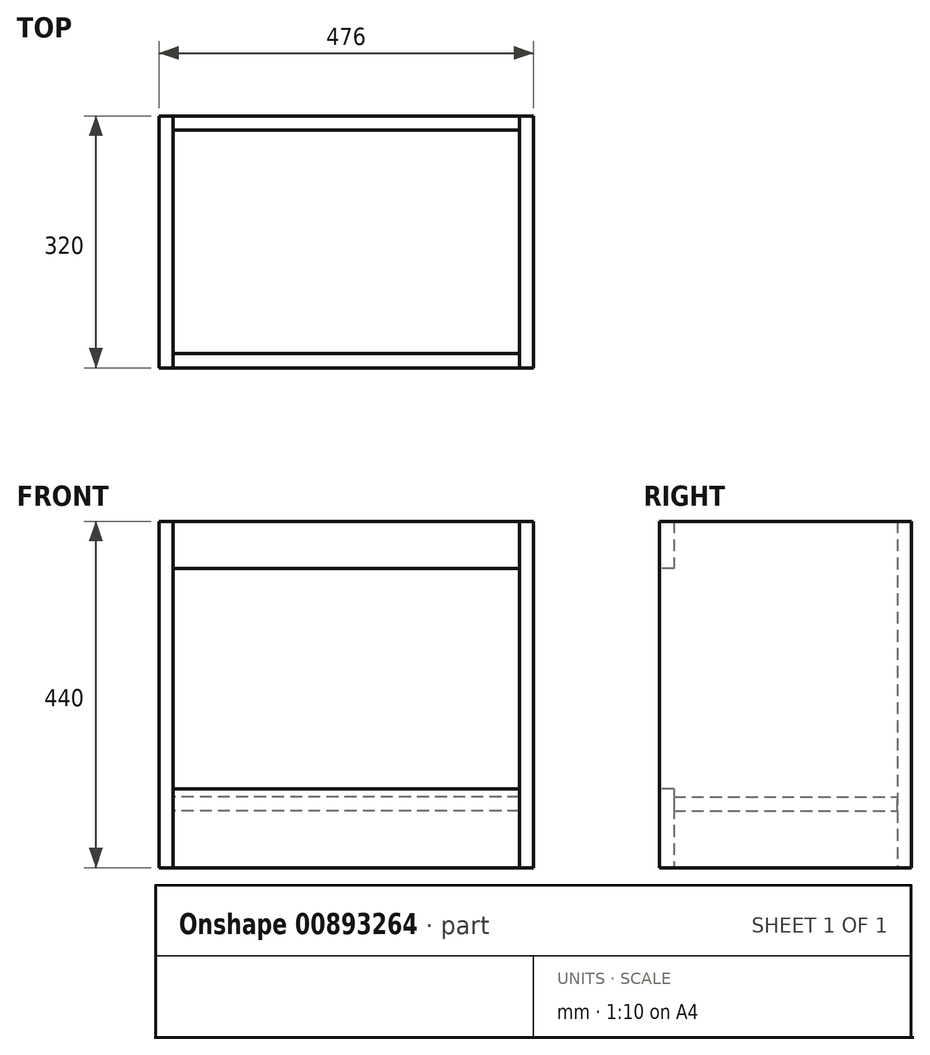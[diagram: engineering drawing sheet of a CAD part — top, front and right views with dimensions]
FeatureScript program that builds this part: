
annotation { "Feature Type Name" : "Feature", "Feature Type Description" : "" }
export const myFeature = defineFeature(function(context is Context, id is Id, definition is map)
    precondition{}
    {
        {
            var Q0;
            Q0=qCreatedBy(makeId("Top.planeOp"),FACE);
            var sketch = newSketch(context, id + "F0", { "sketchPlane" : qUnion([Q0])});
            skLineSegment(sketch, "E0.bottom", {"start": v(150, 100) * mm, "end": v(-150, 100) * mm, "construction": true});
            skLineSegment(sketch, "E0.top", {"start": v(150, -100) * mm, "end": v(-150, -100) * mm, "construction": true});
            skLineSegment(sketch, "E0.left", {"start": v(150, 100) * mm, "end": v(150, -100) * mm, "construction": true});
            skLineSegment(sketch, "E0.right", {"start": v(-150, 100) * mm, "end": v(-150, -100) * mm, "construction": true});
            skPoint(sketch, "E0.middle", {"position": v(0, 0) * mm});
            skLineSegment(sketch, "E1.bottom", {"start": v(-238, -140) * mm, "end": v(-220, -140) * mm});
            skLineSegment(sketch, "E1.top", {"start": v(-238, 180) * mm, "end": v(-220, 180) * mm});
            skLineSegment(sketch, "E1.left", {"start": v(-238, -140) * mm, "end": v(-238, 180) * mm});
            skLineSegment(sketch, "E1.right", {"start": v(-220, -140) * mm, "end": v(-220, 162) * mm});
            skLineSegment(sketch, "E2.MirrorCS", {"start": v(220, -140) * mm, "end": v(220, 162) * mm});
            skLineSegment(sketch, "E3.MirrorCS", {"start": v(238, -140) * mm, "end": v(220, -140) * mm});
            skLineSegment(sketch, "E4.MirrorCS", {"start": v(238, -140) * mm, "end": v(238, 180) * mm});
            skLineSegment(sketch, "E5.MirrorCS", {"start": v(238, 180) * mm, "end": v(220, 180) * mm});
            skLineSegment(sketch, "E6", {"start": v(-220, 180) * mm, "end": v(220, 180) * mm});
            skLineSegment(sketch, "E7", {"start": v(220, 162) * mm, "end": v(-220, 162) * mm});
            skLineSegment(sketch, "E8", {"start": v(-220, 162) * mm, "end": v(-220, 180) * mm});
            skLineSegment(sketch, "E9", {"start": v(220, 162) * mm, "end": v(220, 180) * mm});
            skLineSegment(sketch, "E10", {"start": v(-220, -140) * mm, "end": v(220, -140) * mm, "construction": true});
            skSolve(sketch);
        }
        {
            var Q0;
            Q0=makeQuery(id+"F0.imprint","IMPRINT",FACE,{"disambiguationData":[TD([[makeQuery(id+"F0.imprint","IMPRINT",EDGE,{"derivedFrom":sQuery(id+"F0.wireOp",EDGE,"E6")}),-1.0]])]});
            extrude(context, id + "F1", {"entities" : qUnion([Q0]), "depth" : 120 * mm, "offsetDistance" : 25 * mm, "hasSecondDirection" : true, "secondDirectionOppositeDirection" : true, "secondDirectionDepth" : 320 * mm});
        }
        {
            var Q0;
            Q0=makeQuery(id+"F0.imprint","IMPRINT",FACE,{"disambiguationData":[TD([[makeQuery(id+"F0.imprint","IMPRINT",EDGE,{"derivedFrom":sQuery(id+"F0.wireOp",EDGE,"E1.bottom")}),1.0]])]});
            var Q1;
            Q1=makeQuery(id+"F0.imprint","IMPRINT",FACE,{"disambiguationData":[TD([[makeQuery(id+"F0.imprint","IMPRINT",EDGE,{"derivedFrom":sQuery(id+"F0.wireOp",EDGE,"E2.MirrorCS")}),-1.0]])]});
            var Q2;
            Q2=makeQuery(id+"F1.opExtrude","CAP_FACE",FACE,{"disambiguationData":[OSD([sQuery(id+"F0.wireOp",EDGE,"E6"),sQuery(id+"F0.wireOp",EDGE,"E7"),sQuery(id+"F0.wireOp",EDGE,"E8"),sQuery(id+"F0.wireOp",EDGE,"E9")])],"isStart":false});
            var Q3;
            Q3=makeQuery(id+"F1.opExtrude","CAP_FACE",FACE,{"disambiguationData":[OSD([sQuery(id+"F0.wireOp",EDGE,"E6"),sQuery(id+"F0.wireOp",EDGE,"E7"),sQuery(id+"F0.wireOp",EDGE,"E8"),sQuery(id+"F0.wireOp",EDGE,"E9")])],"isStart":true});
            extrude(context, id + "F2", {"entities" : qUnion([Q0, Q1]), "endBound" : BoundingType.UP_TO_SURFACE, "depth" : 25 * mm, "endBoundEntityFace" : qUnion([Q2]), "offsetDistance" : 25 * mm, "hasSecondDirection" : true, "secondDirectionBound" : SecondDirectionBoundingType.UP_TO_SURFACE, "secondDirectionOppositeDirection" : true, "secondDirectionDepth" : 25 * mm, "secondDirectionBoundEntityFace" : qUnion([Q3])});
        }
        {
            var Q0;
            Q0=qCreatedBy(makeId("Right.planeOp"),FACE);
            var sketch = newSketch(context, id + "F3", { "sketchPlane" : qUnion([Q0])});
            skLineSegment(sketch, "E11.bottom", {"start": v(162, -230) * mm, "end": v(-122, -230) * mm});
            skLineSegment(sketch, "E11.top", {"start": v(162, -248) * mm, "end": v(-122, -248) * mm});
            skLineSegment(sketch, "E11.left", {"start": v(162, -230) * mm, "end": v(162, -248) * mm});
            skLineSegment(sketch, "E12.bottom", {"start": v(-140, -320) * mm, "end": v(-122, -320) * mm});
            skLineSegment(sketch, "E12.top", {"start": v(-140, -220) * mm, "end": v(-122, -220) * mm});
            skLineSegment(sketch, "E12.left", {"start": v(-140, -320) * mm, "end": v(-140, -220) * mm});
            skLineSegment(sketch, "E12.right", {"start": v(-122, -320) * mm, "end": v(-122, -220) * mm});
            skLineSegment(sketch, "E13.bottom", {"start": v(-140, 60) * mm, "end": v(-122, 60) * mm});
            skLineSegment(sketch, "E13.top", {"start": v(-140, 120) * mm, "end": v(-122, 120) * mm});
            skLineSegment(sketch, "E13.left", {"start": v(-140, 60) * mm, "end": v(-140, 120) * mm});
            skLineSegment(sketch, "E13.right", {"start": v(-122, 60) * mm, "end": v(-122, 120) * mm});
            skSolve(sketch);
        }
        {
            var Q0;
            Q0=makeQuery(id+"F3.imprint","IMPRINT",FACE,{"disambiguationData":[TD([[makeQuery(id+"F3.imprint","IMPRINT",EDGE,{"derivedFrom":sQuery(id+"F3.wireOp",EDGE,"E13.bottom")}),1.0]])]});
            var Q1;
            {var subQ2=sQuery(id+"F3.wireOp",EDGE,"E12.bottom");Q1=makeQuery(id+"F3.imprint","IMPRINT",FACE,{"disambiguationData":[TD([[makeQuery(id+"F3.imprint","IMPRINT",EDGE,{"derivedFrom":subQ2}),1.0]])]});}
            var Q2;
            Q2=makeQuery(id+"F2.opExtrude","SWEPT_FACE",FACE,{"disambiguationData":[OSD([sQuery(id+"F0.wireOp",EDGE,"E2.MirrorCS"),sQuery(id+"F0.wireOp",EDGE,"E9")])]});
            var Q3;
            Q3=makeQuery(id+"F2.opExtrude","SWEPT_FACE",FACE,{"disambiguationData":[OSD([sQuery(id+"F0.wireOp",EDGE,"E1.right"),sQuery(id+"F0.wireOp",EDGE,"E8")])]});
            extrude(context, id + "F4", {"entities" : qUnion([Q0, Q1]), "endBound" : BoundingType.UP_TO_SURFACE, "depth" : 25 * mm, "endBoundEntityFace" : qUnion([Q2]), "offsetDistance" : 25 * mm, "hasSecondDirection" : true, "secondDirectionBound" : SecondDirectionBoundingType.UP_TO_SURFACE, "secondDirectionOppositeDirection" : true, "secondDirectionDepth" : 25 * mm, "secondDirectionBoundEntityFace" : qUnion([Q3])});
        }
        {
            var Q0;
            {var subQ0=sQuery(id+"F3.wireOp",EDGE,"E11.bottom");Q0=makeQuery(id+"F3.imprint","IMPRINT",FACE,{"disambiguationData":[TD([[makeQuery(id+"F3.imprint","IMPRINT",EDGE,{"derivedFrom":subQ0}),1.0]])]});}
            var Q1;
            Q1=makeQuery(id+"F2.opExtrude","SWEPT_FACE",FACE,{"disambiguationData":[OSD([sQuery(id+"F0.wireOp",EDGE,"E2.MirrorCS"),sQuery(id+"F0.wireOp",EDGE,"E9")])]});
            var Q2;
            Q2=makeQuery(id+"F2.opExtrude","SWEPT_FACE",FACE,{"disambiguationData":[OSD([sQuery(id+"F0.wireOp",EDGE,"E1.right"),sQuery(id+"F0.wireOp",EDGE,"E8")])]});
            extrude(context, id + "F5", {"entities" : qUnion([Q0]), "endBound" : BoundingType.UP_TO_SURFACE, "depth" : 25 * mm, "endBoundEntityFace" : qUnion([Q1]), "offsetDistance" : 25 * mm, "hasSecondDirection" : true, "secondDirectionBound" : SecondDirectionBoundingType.UP_TO_SURFACE, "secondDirectionOppositeDirection" : true, "secondDirectionDepth" : 25 * mm, "secondDirectionBoundEntityFace" : qUnion([Q2])});
        }
    });
